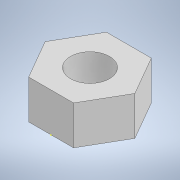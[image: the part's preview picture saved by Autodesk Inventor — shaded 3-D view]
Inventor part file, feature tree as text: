
AUTODESK INVENTOR PART (.ipt)
format: ipt  version: 2020.3 (Build 243373000, 373)  size: 97,792 bytes
history: native  units: in
note: dims shown in document units (in); Inventor stores cm internally (conversion verified against a paired STEP export)
features: sketch x2, extrude x1
ambient origin geometry x8: Origin, YZ Plane, XZ Plane, XY Plane, X Axis, Y Axis, Z Axis, Center Point
bodies: Solid1 (feature_tree)
feature tree (3):
  extrude  "Extrusion1"  Depth=0.5in
  sketch  "Sketch2"  dims[d2=0.5in d3=0.0in]
  sketch  "Sketch1"  dims[d0=1.0in d1=0.5in]
